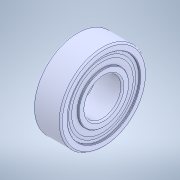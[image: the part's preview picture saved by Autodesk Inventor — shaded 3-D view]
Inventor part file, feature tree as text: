
AUTODESK INVENTOR PART (.ipt)
format: ipt  version: 2020 (Build 240168000, 168)  size: 224,256 bytes
history: native  units: in
note: dims shown in document units (in); Inventor stores cm internally (conversion verified against a paired STEP export)
features: revolve x1
ambient origin geometry x8: Origin, YZ Plane, XZ Plane, XY Plane, X Axis, Y Axis, Z Axis, Center Point
bodies: Solid1 (feature_tree)
feature tree (1):
  revolve  "Revolve1"  [1 undecoded]
note: 1 required parameter value undecoded (feature->parameter linkage not recoverable at this tier; creation-order binding heuristic only, values carry confidence <= 0.55)
